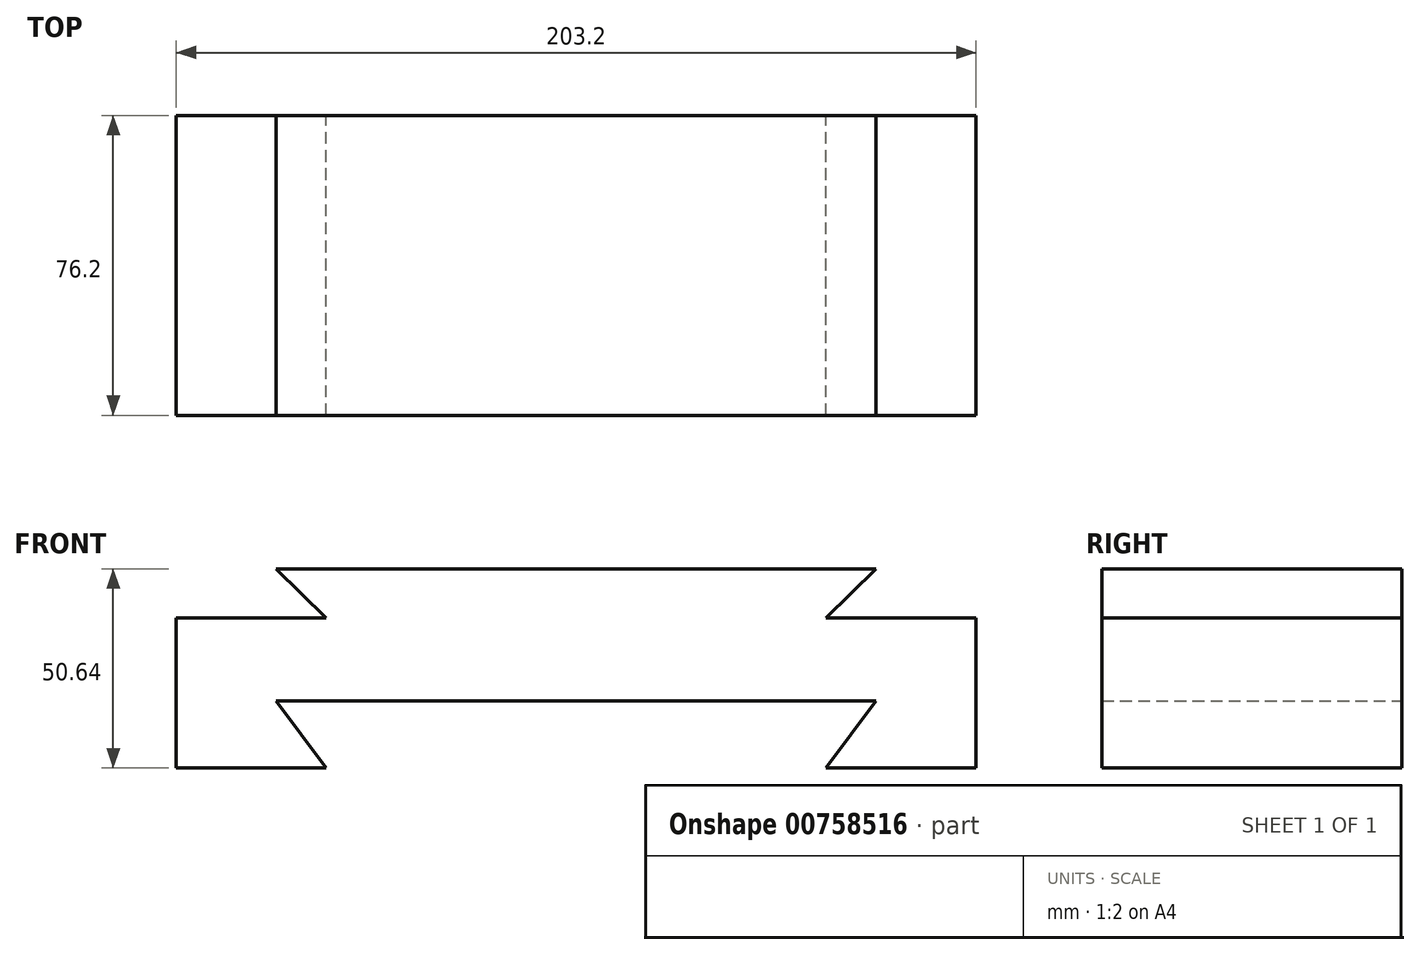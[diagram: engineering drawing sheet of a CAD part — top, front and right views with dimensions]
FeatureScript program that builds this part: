
annotation { "Feature Type Name" : "Feature", "Feature Type Description" : "" }
export const myFeature = defineFeature(function(context is Context, id is Id, definition is map)
    precondition{}
    {
        {
            var Q0;
            Q0=qCreatedBy(makeId("Front.planeOp"),FACE);
            var sketch = newSketch(context, id + "F0", { "sketchPlane" : qUnion([Q0])});
            skLineSegment(sketch, "E0", {"start": v(69.1, -63.12) * mm, "end": v(107.2, -63.12) * mm});
            skLineSegment(sketch, "E1", {"start": v(107.2, -63.12) * mm, "end": v(107.2, -25.02) * mm});
            skLineSegment(sketch, "E2", {"start": v(107.2, -25.02) * mm, "end": v(69.1, -25.02) * mm});
            skLineSegment(sketch, "E3", {"start": v(69.1, -25.02) * mm, "end": v(81.8, -12.48) * mm});
            skLineSegment(sketch, "E4", {"start": v(81.8, -12.48) * mm, "end": v(-70.6, -12.48) * mm});
            skLineSegment(sketch, "E5", {"start": v(-70.6, -12.48) * mm, "end": v(-57.9, -25.02) * mm});
            skLineSegment(sketch, "E6", {"start": v(-57.9, -25.02) * mm, "end": v(-96, -25.02) * mm});
            skLineSegment(sketch, "E7", {"start": v(-96, -25.02) * mm, "end": v(-96, -63.12) * mm});
            skLineSegment(sketch, "E8", {"start": v(-96, -63.12) * mm, "end": v(-57.9, -63.12) * mm});
            skLineSegment(sketch, "E9", {"start": v(-57.9, -63.12) * mm, "end": v(-70.6, -46.07) * mm});
            skLineSegment(sketch, "E10", {"start": v(-70.6, -46.07) * mm, "end": v(81.8, -46.07) * mm});
            skLineSegment(sketch, "E11", {"start": v(81.8, -46.07) * mm, "end": v(69.1, -63.12) * mm});
            skSolve(sketch);
        }
        {
            var Q0;
            Q0 = qSketchRegion(id + "F0", true);
            extrude(context, id + "F1", {"entities" : qUnion([Q0]), "depth" : 76.2 * mm, "offsetDistance" : 25.4 * mm});
        }
    });
